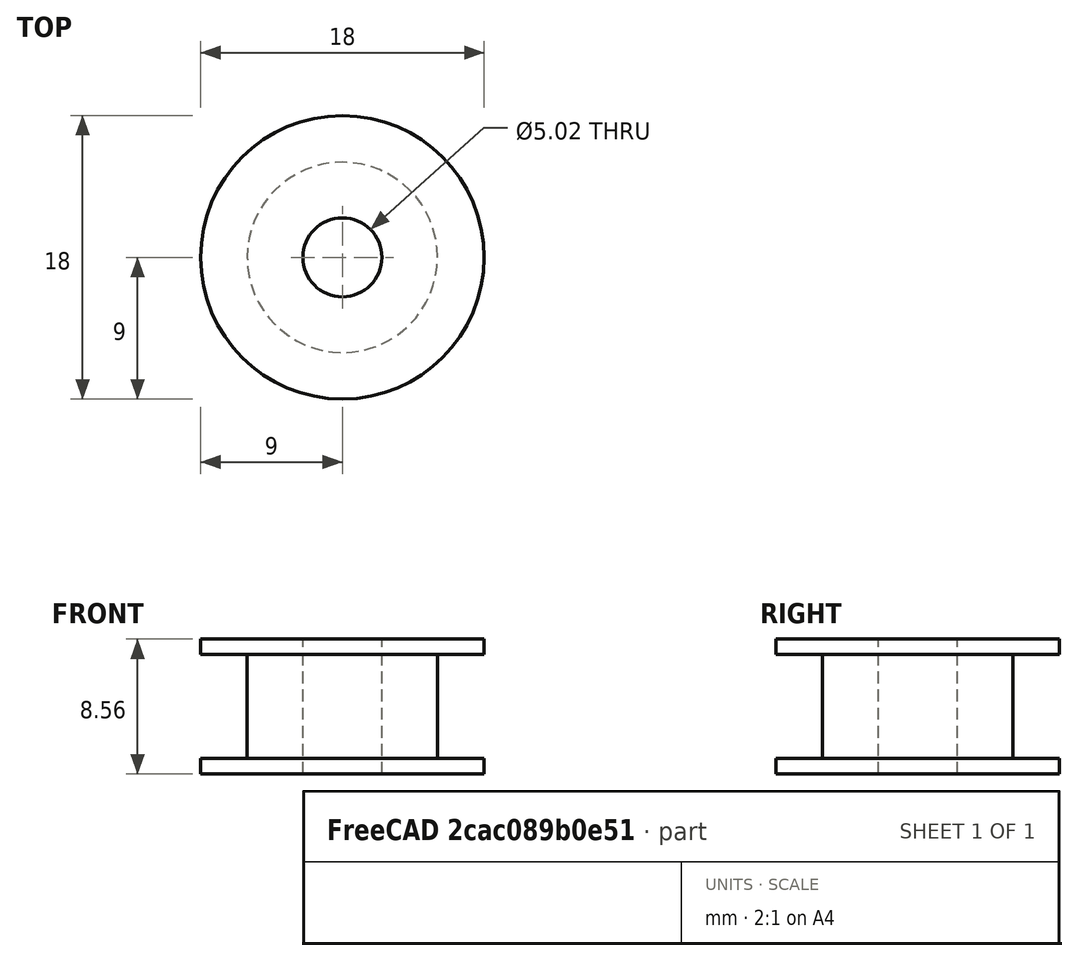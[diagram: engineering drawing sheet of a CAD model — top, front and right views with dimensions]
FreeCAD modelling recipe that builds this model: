
FCSTD DOCUMENT  (FreeCAD 0.20R29410 (Git))
Label: SmoothIdlerPulleyGT2
License: All rights reserved
LicenseURL: http://en.wikipedia.org/wiki/All_rights_reserved
objects: App::DocumentObjectGroup×3, PartDesign::CoordinateSystem×1, App::FeaturePython×1, Sketcher::SketchObject×1, PartDesign::Revolution×1, PartDesign::Body×1, App::Part×1
note: 5 computed .brp shape members not serialized (recipe doc carries the construction recipe); baked Part::Feature solids carry a one-line shape summary decoded from their .brp

FEATURE [App::DocumentObjectGroup] Parts
FEATURE [PartDesign::CoordinateSystem] LCS_Origin
  AttacherType = Attacher::AttachEngine3D
  MapMode = 2
  Support = -> [X_Axis]
FEATURE [App::FeaturePython] Variables  # WARN: FeaturePython — macro-defined, semantics opaque (R4)
  Type = App::PropertyContainer
FEATURE [App::DocumentObjectGroup] Constraints
FEATURE [App::DocumentObjectGroup] Configurations
FEATURE [Sketcher::SketchObject] Sketch
  FullyConstrained = true
  MapMode = 5
  Placement = pos=(0,0,0) rot=(1,0,0;1.5708rad)
  Support = -> [XZ_Plane001]
  sketch-geometry (8):
    g0: LineSegment StartX=2.51 StartY=0 StartZ=0 EndX=2.51 EndY=8.56 EndZ=0
    g1: LineSegment StartX=2.51 StartY=8.56 StartZ=0 EndX=9 EndY=8.56 EndZ=0
    g2: LineSegment StartX=9 StartY=8.56 StartZ=0 EndX=9 EndY=7.58 EndZ=0
    g3: LineSegment StartX=9 StartY=7.58 StartZ=0 EndX=6.045 EndY=7.58 EndZ=0
    g4: LineSegment StartX=6.045 StartY=7.58 StartZ=0 EndX=6.045 EndY=0.98 EndZ=0
    g5: LineSegment StartX=6.045 StartY=0.98 StartZ=0 EndX=9 EndY=0.98 EndZ=0
    g6: LineSegment StartX=9 StartY=0.98 StartZ=0 EndX=9 EndY=0 EndZ=0
    g7: LineSegment StartX=9 StartY=0 StartZ=0 EndX=2.51 EndY=0 EndZ=0
  constraints (24):
    c: PointOnObject(g0,g-1)
    c: Vertical(g0)
    c: Coincident(g0,g1)
    c: Horizontal(g1)
    c: Coincident(g1,g2)
    c: Coincident(g2,g3)
    c: Horizontal(g3)
    c: Coincident(g3,g4)
    c: Vertical(g4)
    c: Coincident(g4,g5)
    c: Horizontal(g5)
    c: Coincident(g5,g6)
    c: PointOnObject(g6,g-1)
    c: Vertical(g6)
    c: Coincident(g6,g7)
    c: Coincident(g7,g0)
    c: Vertical(g2)
    c: DistanceX(g-1,g3) = 6.045
    c: DistanceX(g-1,g0) = 2.51
    c: DistanceY(g4,g4) = 6.6
    c: PointOnObject(g2,g6)
    c: DistanceX(g-1,g6) = 9
    c: DistanceY(g-1,g0) = 8.56
    c: Equal(g2,g6)
FEATURE [PartDesign::Revolution] Revolution
  Angle = 360
  Axis = (0,-2e-16,1)
  Base = (0,0,0)
  Placement = pos=(0,0,0) rot=(1,0,0;1.5708rad)
  Profile = -> Sketch
  ReferenceAxis = -> Sketch [V_Axis]
  Reversed = true
FEATURE [PartDesign::Body] Body
  Group = -> [Sketch,Revolution]
  Origin = -> Origin001
  Tip = -> Revolution
FEATURE [App::Part] Assembly
  AssemblyType = Part::Link
  Group = -> [LCS_Origin,Variables,Constraints,Configurations,Body]
  Origin = -> Origin
  Type = Assembly
